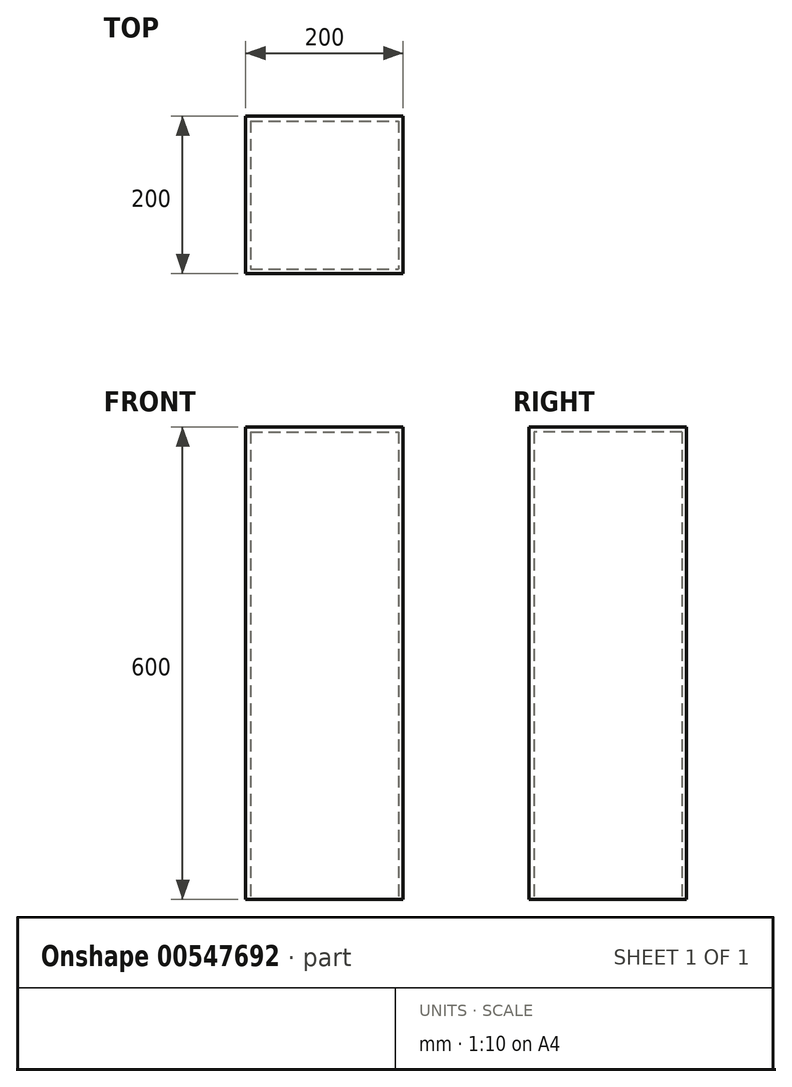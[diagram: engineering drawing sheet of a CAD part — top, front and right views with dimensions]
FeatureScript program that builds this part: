
annotation { "Feature Type Name" : "Feature", "Feature Type Description" : "" }
export const myFeature = defineFeature(function(context is Context, id is Id, definition is map)
    precondition{}
    {
        {
            var Q0;
            Q0=qCreatedBy(makeId("Top.planeOp"),FACE);
            var sketch = newSketch(context, id + "F0", { "sketchPlane" : qUnion([Q0])});
            skLineSegment(sketch, "E0.bottom", {"start": v(-100, 100) * mm, "end": v(100, 100) * mm});
            skLineSegment(sketch, "E0.top", {"start": v(-100, -100) * mm, "end": v(100, -100) * mm});
            skLineSegment(sketch, "E0.left", {"start": v(-100, 100) * mm, "end": v(-100, -100) * mm});
            skLineSegment(sketch, "E0.right", {"start": v(100, 100) * mm, "end": v(100, -100) * mm});
            skPoint(sketch, "E1", {"position": v(-100, 0) * mm});
            skPoint(sketch, "E2", {"position": v(0, 100) * mm});
            skSolve(sketch);
        }
        {
            var Q0;
            Q0 = qSketchRegion(id + "F0", true);
            extrude(context, id + "F1", {"entities" : qUnion([Q0]), "depth" : 600 * mm, "offsetDistance" : 25 * mm});
        }
        {
            var Q0;
            Q0=makeQuery(id+"F1.opExtrude","CAP_FACE",FACE,{"disambiguationData":[OSD([sQuery(id+"F0.wireOp",EDGE,"E0.bottom"),sQuery(id+"F0.wireOp",EDGE,"E0.top"),sQuery(id+"F0.wireOp",EDGE,"E0.left"),sQuery(id+"F0.wireOp",EDGE,"E0.right")])],"isStart":true});
            shell(context, id + "F2", {"entities" : qUnion([Q0]), "thickness" : 6 * mm});
        }
        {
            var Q0;
            Q0=makeQuery(id+"F1.opExtrude","CAP_FACE",FACE,{"disambiguationData":[OSD([sQuery(id+"F0.wireOp",EDGE,"E0.bottom"),sQuery(id+"F0.wireOp",EDGE,"E0.top"),sQuery(id+"F0.wireOp",EDGE,"E0.left"),sQuery(id+"F0.wireOp",EDGE,"E0.right")])],"isStart":false});
            var sketch = newSketch(context, id + "F3", { "sketchPlane" : qUnion([Q0])});
            skLineSegment(sketch, "E3", {"start": v(100, -100) * mm, "end": v(200, 0) * mm});
            skSolve(sketch);
        }
        {
            var Q0;
            Q0=makeQuery(id+"F3.imprint","IMPRINT",FACE,{"disambiguationData":[TD([[makeQuery(id+"F3.imprint","IMPRINT",EDGE,{"derivedFrom":makeQuery(id+"F1.opExtrude","CAP_EDGE",EDGE,{"disambiguationData":[OSD([sQuery(id+"F0.wireOp",EDGE,"E0.bottom")])],"isStart":false})}),-1.0]])]});
            var Q1;
            Q1=sQuery(id+"F3.wireOp",EDGE,"E3");
            cPlane(context, id + "F4", {"entities" : qUnion([Q0, Q1]), "cplaneType" : CPlaneType.LINE_ANGLE, "offset" : 25 * mm, "angle" : 45 * degree, "width" : 150 * mm, "height" : 150 * mm});
        }
    });
